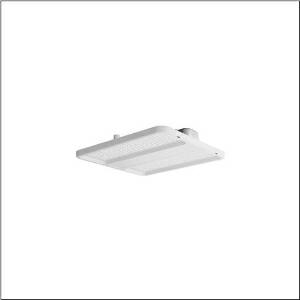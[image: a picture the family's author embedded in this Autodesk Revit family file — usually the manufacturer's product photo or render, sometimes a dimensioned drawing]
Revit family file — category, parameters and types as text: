
# Revit family: highbay_21_midi_52hn11da4fda
name_source: partatom
category: Lighting Fixtures
units: mm (PartAtom-declared; Revit-internal decimal feet)

## family parameters
Cut with Voids When Loaded = No
Host = Face
Light Source = No
Part Type = Normal
Room Calculation Point = No
Round Connector Dimension = Use Diameter
Shared = No

## types (1)
- --- (1 x LED, 2110 lm, 11.9 W, 4000K)
    Apparent Load = 12 VA
    CIE Flux Codes = 89 97 99 100 100
    Color Rendering = 80
    Color Temperature = 4000K
    Default Elevation = 1800 mm
    Description = high bay luminaire Highbay 21 midi; direct symmetric narrow distribution, light control with lens of PMMA; UGR ≤ 19 (X = 4H | Y = 8H | S = 0.25H | reflection values 70/50/20); luminous flux: 14.000lm; light colour: 840, colour temperature: 4000K, MacAdam ≤ 3 SDCM (initial), colour rendering: CRI > 80; luminous efficacy: 194,2lm/W; rated service life: 75.000h (L80/B50) at AT= ta max; control: DALI 2; housing frame of high-performance plastic PA6, matt traffic white (RAL 9016); cover of PMMA; dimension (LxWxH): 474 x 442 x 72mm; luminaire connection: terminal, 5-pole, max. 2.5mm² (cable entry for one cable, Ø 8.5..16mm); mains connection: 230..240V, AC/DC 0/50..60Hz; connected load: 72,1W; protection rating (complete): IP66; insulation class (complete): insulation class I (protective earthing); protection symbol: D; impact resistance: IK08; halogen-free wiring; for central battery installations according to DIN EN 60598-2-22; LABS conformity tested according to VDMA 24364:2018-05; corresponds to IFS (International Featured Standards) requirements for safety and quality in the food industry; certification: CE, ENEC, VDE, UKCA; permissible operating ambient temperature: -40..+70°C (reducing of maximum allowable ambient temperature of 5°C with ceiling mounting); packaging unit: 1 piece; (delivery without accessories; please order mounting accessories separately)
    Height = 72 mm  [stored 0.23622 ft]
    Lamp = 1 x LED
    Lamp Light Flux = 2110 lm
    Lamp Power = 11.9 W
    Lamp count = 1
    Length = 474 mm
    Luminous efficacy = 177 lm/W
    Manufacturer = Siteco
    ModVariant = No
    Model = 52HN11DA4FDA
    Mounting Place = Ceiling
    Mounting Type = Pendant
    Number of Poles = 1
    OnlyDefault = Yes
    Power Factor = 1
    Product Name = Highbay 21 midi
    Product group = high bay luminaire
    ProductGroupID = 901
    Protection Class = Protection class I
    Protection Degree = IP 66
    RLX_Detail_Level = 1
    RLX_Emergency_Light_Flux = 0 lm
    RLX_Emergency_Type = 0
    RLX_Emergency_Type_DB = No
    RlxData = <blob elided: 17549 chars, md5=bc848fbc>
    Socket = socket
    Standby Power = 0 W
    System Light Flux = 2110 lm
    System Power = 12 W
    Type Comments = : DC mode (central or group accumulator) initial emergency light level
    Type Image = l_1363240.jpg
    URL = http://relux.com
    VarID = @adj_000179
    Voltage = 0 V
    Weight = 0.00 kg
    Width = 442 mm

note: [stored X ft] marks values corroborated as IEEE doubles in the binary element streams (Revit-internal decimal feet)

## geometry (parser evidence)
native form markers: Blend x4, Sweep x10
no freeform markers — native parametric forms only
